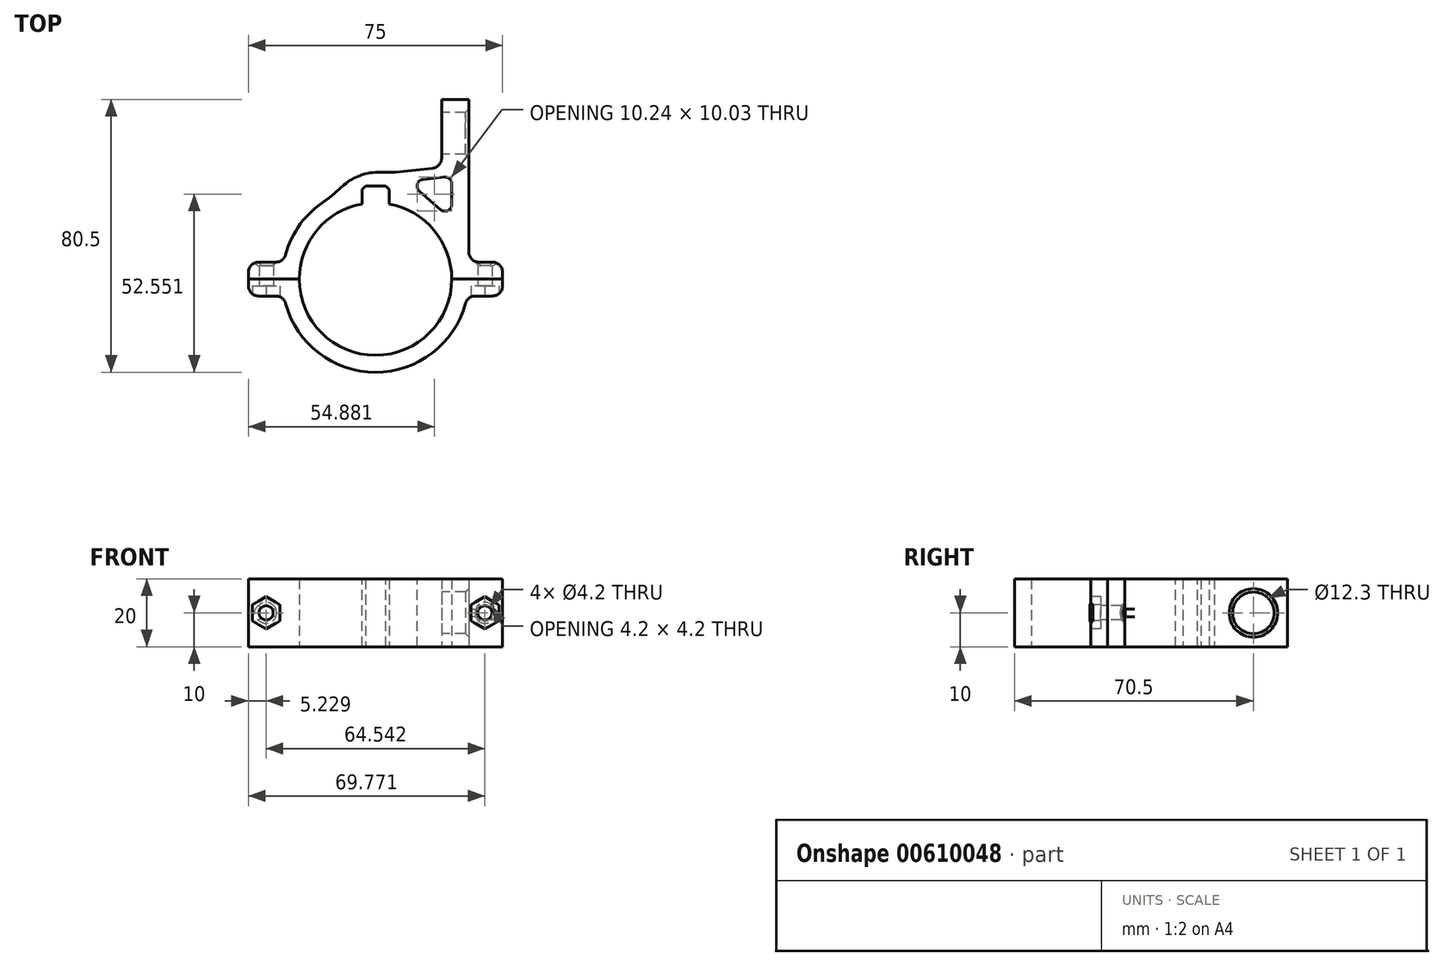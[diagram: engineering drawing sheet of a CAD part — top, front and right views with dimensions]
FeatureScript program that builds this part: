
annotation { "Feature Type Name" : "Feature", "Feature Type Description" : "" }
export const myFeature = defineFeature(function(context is Context, id is Id, definition is map)
    precondition{}
    {
        {
            var Q0;
            Q0=qCreatedBy(makeId("Top.planeOp"),FACE);
            var sketch = newSketch(context, id + "F0", { "sketchPlane" : qUnion([Q0])});
            skArc(sketch, "E0", {"start": v(-4, 22.14) * mm, "mid": v(0, -22.5) * mm, "end": v(4, 22.14) * mm});
            skArc(sketch, "E1", {"start": v(-4, 27.2) * mm, "mid": v(-19.08, 19.8) * mm, "end": v(-27.04, 5) * mm});
            skLineSegment(sketch, "E2.top", {"start": v(-4, 27.5) * mm, "end": v(4, 27.5) * mm});
            skLineSegment(sketch, "E2.left", {"start": v(-4, 22.14) * mm, "end": v(-4, 27.5) * mm});
            skLineSegment(sketch, "E2.right", {"start": v(4, 22.14) * mm, "end": v(4, 27.5) * mm});
            skPoint(sketch, "E2.middle", {"position": v(0, 22.5) * mm});
            skLineSegment(sketch, "E3", {"start": v(-14.06, 23.63) * mm, "end": v(-5, 31.5) * mm});
            skLineSegment(sketch, "E4", {"start": v(-5, 31.5) * mm, "end": v(5, 31.5) * mm});
            skLineSegment(sketch, "E5", {"start": v(5, 31.5) * mm, "end": v(14.06, 23.63) * mm});
            skPoint(sketch, "E6", {"position": v(0, 31.5) * mm});
            skLineSegment(sketch, "E7", {"start": v(27.5, 5) * mm, "end": v(27.5, 53) * mm});
            skLineSegment(sketch, "E8", {"start": v(27.5, 53) * mm, "end": v(19.5, 53) * mm});
            skLineSegment(sketch, "E9", {"start": v(19.5, 53) * mm, "end": v(19.5, 33) * mm});
            skLineSegment(sketch, "E10", {"start": v(19.5, 33) * mm, "end": v(5, 31.5) * mm});
            skLineSegment(sketch, "E11", {"start": v(22.5, 17.63) * mm, "end": v(22.5, 30.3) * mm});
            skLineSegment(sketch, "E12", {"start": v(22.5, 30.3) * mm, "end": v(9.47, 28.95) * mm});
            skLineSegment(sketch, "E13", {"start": v(9.47, 28.95) * mm, "end": v(22.5, 17.63) * mm});
            skPoint(sketch, "E14", {"position": v(-4, 22.14) * mm});
            skPoint(sketch, "E15", {"position": v(4, 22.14) * mm});
            skLineSegment(sketch, "E16", {"start": v(-22.5, 0) * mm, "end": v(-27.5, 0) * mm});
            skLineSegment(sketch, "E17", {"start": v(-27.5, 0) * mm, "end": v(-37.5, 0) * mm});
            skLineSegment(sketch, "E18", {"start": v(-37.5, 0) * mm, "end": v(-37.5, 5) * mm});
            skLineSegment(sketch, "E19", {"start": v(-37.5, 5) * mm, "end": v(-27.04, 5) * mm});
            skLineSegment(sketch, "E20", {"start": v(22.5, 0) * mm, "end": v(27.5, 0) * mm});
            skLineSegment(sketch, "E21", {"start": v(37.5, 0) * mm, "end": v(37.5, 5) * mm});
            skLineSegment(sketch, "E22", {"start": v(37.5, 5) * mm, "end": v(27.5, 5) * mm});
            skLineSegment(sketch, "E23", {"start": v(27.5, 0) * mm, "end": v(37.5, 0) * mm});
            skLineSegment(sketch, "E24.MirrorCS", {"start": v(-37.5, 0) * mm, "end": v(-37.5, -5) * mm});
            skLineSegment(sketch, "E25.MirrorCS", {"start": v(-37.5, -5) * mm, "end": v(-27.04, -5) * mm});
            skLineSegment(sketch, "E26.MirrorCS", {"start": v(37.5, 0) * mm, "end": v(37.5, -5) * mm});
            skLineSegment(sketch, "E27", {"start": v(37.5, -5) * mm, "end": v(27.04, -5) * mm});
            skArc(sketch, "E28.trimOffspring", {"start": v(-27.04, -5) * mm, "mid": v(0, -27.5) * mm, "end": v(27.04, -5) * mm});
            skArc(sketch, "E29.trimOffspring", {"start": v(27.5, 0) * mm, "mid": v(20.81, 17.98) * mm, "end": v(4, 27.2) * mm});
            skSolve(sketch);
        }
        {
            var Q0;
            {var subQ7=sQuery(id+"F0.wireOp",EDGE,"E16");Q0=makeQuery(id+"F0.imprint","IMPRINT",FACE,{"disambiguationData":[TD([[makeQuery(id+"F0.imprint","IMPRINT",EDGE,{"derivedFrom":subQ7}),-1.0]])]});}
            var Q1;
            {var subQ1=sQuery(id+"F0.wireOp",EDGE,"E2.top");Q1=makeQuery(id+"F0.imprint","IMPRINT",FACE,{"disambiguationData":[TD([[makeQuery(id+"F0.imprint","IMPRINT",EDGE,{"derivedFrom":subQ1}),1.0]])]});}
            var Q2;
            {var subQ0=sQuery(id+"F0.wireOp",EDGE,"E20");Q2=makeQuery(id+"F0.imprint","IMPRINT",FACE,{"disambiguationData":[TD([[makeQuery(id+"F0.imprint","IMPRINT",EDGE,{"derivedFrom":subQ0}),1.0]])]});}
            var Q3;
            {var subQ0=sQuery(id+"F0.wireOp",EDGE,"E5");Q3=makeQuery(id+"F0.imprint","IMPRINT",FACE,{"disambiguationData":[TD([[makeQuery(id+"F0.imprint","IMPRINT",EDGE,{"derivedFrom":subQ0}),1.0]])]});}
            extrude(context, id + "F1", {"entities" : qUnion([Q0, Q1, Q2, Q3]), "depth" : 20 * mm, "offsetDistance" : 25 * mm});
        }
        {
            var Q0;
            {var subQ1=sQuery(id+"F0.wireOp",EDGE,"E16");Q0=makeQuery(id+"F0.imprint","IMPRINT",FACE,{"disambiguationData":[TD([[makeQuery(id+"F0.imprint","IMPRINT",EDGE,{"derivedFrom":subQ1}),1.0]])]});}
            extrude(context, id + "F2", {"entities" : qUnion([Q0]), "depth" : 20 * mm, "offsetDistance" : 25 * mm});
        }
        {
            var Q0;
            Q0=makeQuery(id+"F2.opExtrude","SWEPT_FACE",FACE,{"disambiguationData":[OSD([sQuery(id+"F0.wireOp",EDGE,"E25.MirrorCS")])]});
            var sketch = newSketch(context, id + "F3", { "sketchPlane" : qUnion([Q0])});
            skPoint(sketch, "E30", {"position": v(-32.27, 10) * mm});
            skPoint(sketch, "E30.positionSnap0", {"position": v(-32.27, 20) * mm});
            skPoint(sketch, "E30.positionSnap1", {"position": v(-37.5, 10) * mm});
            skCircle(sketch, "E31.cCircle", {"center": v(-32.27, 10) * mm, "radius": 4.1 * mm, "construction": true});
            skPoint(sketch, "E31.cCircle.perimeterSnap0", {"position": v(-27.04, 10) * mm});
            skLineSegment(sketch, "E31.0", {"start": v(-28.17, 12.37) * mm, "end": v(-28.17, 7.63) * mm});
            skLineSegment(sketch, "E31.1", {"start": v(-28.17, 7.63) * mm, "end": v(-32.27, 5.27) * mm});
            skLineSegment(sketch, "E31.2", {"start": v(-32.27, 5.27) * mm, "end": v(-36.37, 7.63) * mm});
            skLineSegment(sketch, "E31.3", {"start": v(-36.37, 7.63) * mm, "end": v(-36.37, 12.37) * mm});
            skLineSegment(sketch, "E31.4", {"start": v(-36.37, 12.37) * mm, "end": v(-32.27, 14.73) * mm});
            skLineSegment(sketch, "E31.5", {"start": v(-32.27, 14.73) * mm, "end": v(-28.17, 12.37) * mm});
            skPoint(sketch, "E31.0.midPoint", {"position": v(-28.17, 10) * mm});
            skPoint(sketch, "E31.0.midPoint.positionSnap0", {"position": v(-27.04, 10) * mm});
            skCircle(sketch, "E32", {"center": v(-32.27, 10) * mm, "radius": 2.1 * mm});
            skPoint(sketch, "E33.MirrorP", {"position": v(27.04, 10) * mm});
            skPoint(sketch, "E34.MirrorP", {"position": v(37.5, 10) * mm});
            skCircle(sketch, "E35.MirrorC", {"center": v(32.27, 10) * mm, "radius": 4.1 * mm, "construction": true});
            skLineSegment(sketch, "E36.MirrorCS", {"start": v(28.17, 12.37) * mm, "end": v(28.17, 7.63) * mm});
            skLineSegment(sketch, "E37.MirrorCS", {"start": v(28.17, 7.63) * mm, "end": v(32.27, 5.27) * mm});
            skLineSegment(sketch, "E38.MirrorCS", {"start": v(32.27, 5.27) * mm, "end": v(36.37, 7.63) * mm});
            skLineSegment(sketch, "E39.MirrorCS", {"start": v(36.37, 7.63) * mm, "end": v(36.37, 12.37) * mm});
            skLineSegment(sketch, "E40.MirrorCS", {"start": v(36.37, 12.37) * mm, "end": v(32.27, 14.73) * mm});
            skLineSegment(sketch, "E41.MirrorCS", {"start": v(32.27, 14.73) * mm, "end": v(28.17, 12.37) * mm});
            skPoint(sketch, "E42.MirrorP", {"position": v(28.17, 10) * mm});
            skCircle(sketch, "E43.MirrorC", {"center": v(32.27, 10) * mm, "radius": 2.1 * mm});
            skSolve(sketch);
        }
        {
            var Q0;
            Q0=makeQuery(id+"F1.opExtrude","SWEPT_FACE",FACE,{"disambiguationData":[OSD([sQuery(id+"F0.wireOp",EDGE,"E9")])]});
            var sketch = newSketch(context, id + "F4", { "sketchPlane" : qUnion([Q0])});
            skCircle(sketch, "E44", {"center": v(-43, 10) * mm, "radius": 6.15 * mm});
            skPoint(sketch, "E44.centerSnap0", {"position": v(-43, 20) * mm});
            skPoint(sketch, "E44.centerSnap1", {"position": v(-53, 10) * mm});
            skSolve(sketch);
        }
        {
            var Q0;
            Q0=makeQuery(id+"F3.imprint","IMPRINT",FACE,{"disambiguationData":[TD([[makeQuery(id+"F3.imprint","IMPRINT",EDGE,{"derivedFrom":sQuery(id+"F3.wireOp",EDGE,"E31.0")}),-1.0]])]});
            var Q1;
            Q1=makeQuery(id+"F3.imprint","IMPRINT",FACE,{"disambiguationData":[TD([[makeQuery(id+"F3.imprint","IMPRINT",EDGE,{"derivedFrom":sQuery(id+"F3.wireOp",EDGE,"E36.MirrorCS")}),1.0]])]});
            extrude(context, id + "F5", {"entities" : qUnion([Q0, Q1]), "operationType" : NewBodyOperationType.REMOVE, "oppositeDirection" : true, "depth" : 3 * mm, "offsetDistance" : 25 * mm});
        }
        {
            var Q0;
            Q0=makeQuery(id+"F5.boolean.opBoolean","SPLIT",FACE,{"disambiguationData":[TD([makeQuery(id+"F5.opExtrude","SWEPT_FACE",FACE,{"disambiguationData":[OSD([sQuery(id+"F3.wireOp",EDGE,"E32")])]})])],"derivedFrom":makeQuery(id+"F2.opExtrude","SWEPT_FACE",FACE,{"disambiguationData":[OSD([sQuery(id+"F0.wireOp",EDGE,"E25.MirrorCS")])]})});
            var Q1;
            Q1=makeQuery(id+"F5.boolean.opBoolean","SPLIT",FACE,{"disambiguationData":[TD([makeQuery(id+"F5.opExtrude","SWEPT_FACE",FACE,{"disambiguationData":[OSD([sQuery(id+"F3.wireOp",EDGE,"E43.MirrorC")])]})])],"derivedFrom":makeQuery(id+"F2.opExtrude","SWEPT_FACE",FACE,{"disambiguationData":[OSD([sQuery(id+"F0.wireOp",EDGE,"E27")])]})});
            extrude(context, id + "F6", {"entities" : qUnion([Q0, Q1]), "operationType" : NewBodyOperationType.REMOVE, "oppositeDirection" : true, "depth" : 25 * mm, "offsetDistance" : 25 * mm});
        }
        {
            var Q0;
            Q0=makeQuery(id+"F4.imprint","IMPRINT",FACE,{"disambiguationData":[TD([[makeQuery(id+"F4.imprint","IMPRINT",EDGE,{"derivedFrom":sQuery(id+"F4.wireOp",EDGE,"E44")}),1.0]])]});
            extrude(context, id + "F7", {"entities" : qUnion([Q0]), "operationType" : NewBodyOperationType.REMOVE, "oppositeDirection" : true, "depth" : 25 * mm, "offsetDistance" : 25 * mm});
        }
        {
            var Q0;
            Q0=makeQuery(id+"F1.opExtrude","SWEPT_EDGE",EDGE,{"disambiguationData":[OSD([sQuery(id+"F0.wireOp",EDGE,"E1"),sQuery(id+"F0.wireOp",EDGE,"E3")])]});
            var Q1;
            Q1=makeQuery(id+"F1.opExtrude","SWEPT_EDGE",EDGE,{"disambiguationData":[OSD([sQuery(id+"F0.wireOp",EDGE,"E3"),sQuery(id+"F0.wireOp",EDGE,"E4")])]});
            var Q2;
            Q2=makeQuery(id+"F1.opExtrude","SWEPT_EDGE",EDGE,{"disambiguationData":[OSD([sQuery(id+"F0.wireOp",EDGE,"E4"),sQuery(id+"F0.wireOp",EDGE,"E5"),sQuery(id+"F0.wireOp",EDGE,"E10")])]});
            fillet(context, id + "F8", {"entities" : qUnion([Q0, Q1, Q2]), "radius" : 15 * mm, "tangentPropagation" : true, "allowEdgeOverflow" : false});
        }
        {
            var Q0;
            Q0=makeQuery(id+"F1.opExtrude","SWEPT_EDGE",EDGE,{"disambiguationData":[OSD([sQuery(id+"F0.wireOp",EDGE,"E9"),sQuery(id+"F0.wireOp",EDGE,"E10")])]});
            var Q1;
            Q1=makeQuery(id+"F1.opExtrude","SWEPT_EDGE",EDGE,{"disambiguationData":[OSD([sQuery(id+"F0.wireOp",EDGE,"E1"),sQuery(id+"F0.wireOp",EDGE,"E19")])]});
            var Q2;
            Q2=makeQuery(id+"F1.opExtrude","SWEPT_EDGE",EDGE,{"disambiguationData":[OSD([sQuery(id+"F0.wireOp",EDGE,"E7"),sQuery(id+"F0.wireOp",EDGE,"E22")])]});
            var Q3;
            Q3=makeQuery(id+"F2.opExtrude","SWEPT_EDGE",EDGE,{"disambiguationData":[OSD([sQuery(id+"F0.wireOp",EDGE,"E27"),sQuery(id+"F0.wireOp",EDGE,"E28.trimOffspring")])]});
            var Q4;
            Q4=makeQuery(id+"F2.opExtrude","SWEPT_EDGE",EDGE,{"disambiguationData":[OSD([sQuery(id+"F0.wireOp",EDGE,"E26.MirrorCS"),sQuery(id+"F0.wireOp",EDGE,"E27")])]});
            var Q5;
            Q5=makeQuery(id+"F1.opExtrude","SWEPT_EDGE",EDGE,{"disambiguationData":[OSD([sQuery(id+"F0.wireOp",EDGE,"E21"),sQuery(id+"F0.wireOp",EDGE,"E22")])]});
            var Q6;
            Q6=makeQuery(id+"F2.opExtrude","SWEPT_EDGE",EDGE,{"disambiguationData":[OSD([sQuery(id+"F0.wireOp",EDGE,"E25.MirrorCS"),sQuery(id+"F0.wireOp",EDGE,"E28.trimOffspring")])]});
            var Q7;
            Q7=makeQuery(id+"F2.opExtrude","SWEPT_EDGE",EDGE,{"disambiguationData":[OSD([sQuery(id+"F0.wireOp",EDGE,"E24.MirrorCS"),sQuery(id+"F0.wireOp",EDGE,"E25.MirrorCS")])]});
            var Q8;
            Q8=makeQuery(id+"F1.opExtrude","SWEPT_EDGE",EDGE,{"disambiguationData":[OSD([sQuery(id+"F0.wireOp",EDGE,"E18"),sQuery(id+"F0.wireOp",EDGE,"E19")])]});
            fillet(context, id + "F9", {"entities" : qUnion([Q0, Q1, Q2, Q3, Q4, Q5, Q6, Q7, Q8]), "radius" : 3 * mm, "tangentPropagation" : true, "allowEdgeOverflow" : false});
        }
        {
            var Q0;
            Q0=makeQuery(id+"F7.boolean.opBoolean","COPY",EDGE,{"derivedFrom":makeQuery(id+"F7.opExtrude","CAP_EDGE",EDGE,{"disambiguationData":[OSD([sQuery(id+"F4.wireOp",EDGE,"E44")])],"isStart":true})});
            var Q1;
            Q1=makeQuery(id+"F7.boolean.opBoolean","INTERSECT",EDGE,{"derivedFrom":[makeQuery(id+"F1.opExtrude","SWEPT_FACE",FACE,{"disambiguationData":[OSD([sQuery(id+"F0.wireOp",EDGE,"E7")])]}),makeQuery(id+"F7.opExtrude","SWEPT_FACE",FACE,{"disambiguationData":[OSD([sQuery(id+"F4.wireOp",EDGE,"E44")])]})]});
            var Q2;
            Q2=makeQuery(id+"F6.boolean.opBoolean","INTERSECT",EDGE,{"derivedFrom":[makeQuery(id+"F1.opExtrude","SWEPT_FACE",FACE,{"disambiguationData":[OSD([sQuery(id+"F0.wireOp",EDGE,"E22")])]}),makeQuery(id+"F6.opExtrude","SWEPT_FACE",FACE,{"disambiguationData":[OSD([sQuery(id+"F3.wireOp",EDGE,"E43.MirrorC")])]})]});
            var Q3;
            Q3=makeQuery(id+"F6.boolean.opBoolean","INTERSECT",EDGE,{"derivedFrom":[makeQuery(id+"F1.opExtrude","SWEPT_FACE",FACE,{"disambiguationData":[OSD([sQuery(id+"F0.wireOp",EDGE,"E19")])]}),makeQuery(id+"F6.opExtrude","SWEPT_FACE",FACE,{"disambiguationData":[OSD([sQuery(id+"F3.wireOp",EDGE,"E32")])]})]});
            var Q4;
            Q4=makeQuery(id+"F1.opExtrude","SWEPT_EDGE",EDGE,{"disambiguationData":[OSD([sQuery(id+"F0.wireOp",EDGE,"E2.top"),sQuery(id+"F0.wireOp",EDGE,"E2.left")])]});
            var Q5;
            Q5=makeQuery(id+"F1.opExtrude","SWEPT_EDGE",EDGE,{"disambiguationData":[OSD([sQuery(id+"F0.wireOp",EDGE,"E2.top"),sQuery(id+"F0.wireOp",EDGE,"E2.right")])]});
            chamfer(context, id + "F10", {"entities" : qUnion([Q0, Q1, Q2, Q3, Q4, Q5]), "width" : 1 * mm, "tangentPropagation" : true});
        }
        {
            var Q0;
            Q0=makeQuery(id+"F1.opExtrude","SWEPT_EDGE",EDGE,{"disambiguationData":[OSD([sQuery(id+"F0.wireOp",EDGE,"E12"),sQuery(id+"F0.wireOp",EDGE,"E13")])]});
            var Q1;
            Q1=makeQuery(id+"F1.opExtrude","SWEPT_EDGE",EDGE,{"disambiguationData":[OSD([sQuery(id+"F0.wireOp",EDGE,"E11"),sQuery(id+"F0.wireOp",EDGE,"E13")])]});
            var Q2;
            Q2=makeQuery(id+"F1.opExtrude","SWEPT_EDGE",EDGE,{"disambiguationData":[OSD([sQuery(id+"F0.wireOp",EDGE,"E11"),sQuery(id+"F0.wireOp",EDGE,"E12")])]});
            fillet(context, id + "F11", {"entities" : qUnion([Q0, Q1, Q2]), "radius" : 2 * mm, "tangentPropagation" : true, "allowEdgeOverflow" : false});
        }
    });
